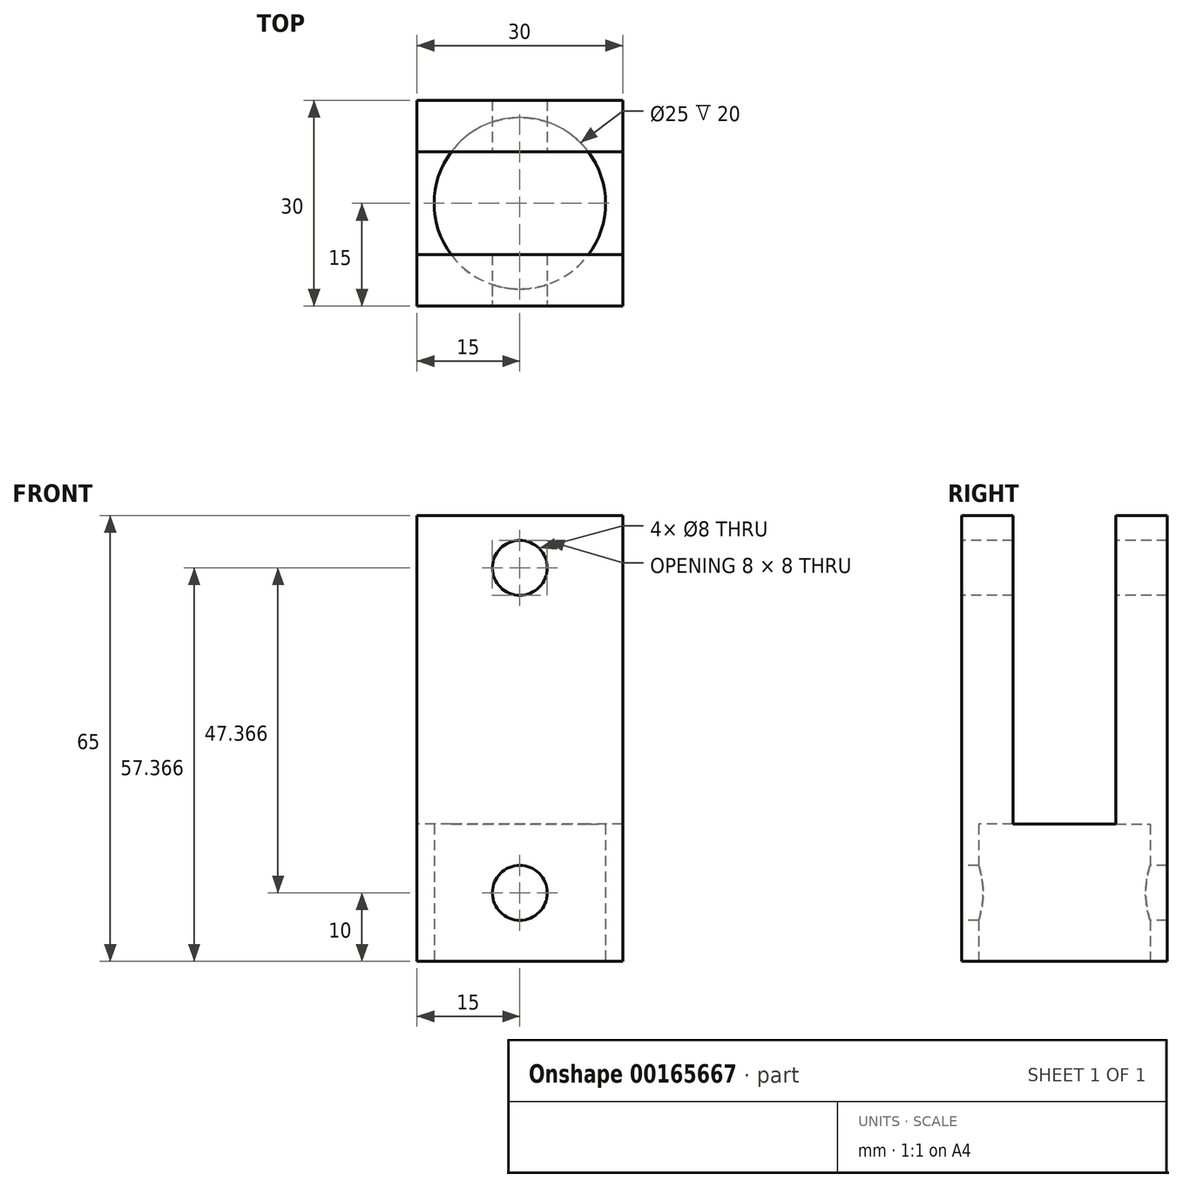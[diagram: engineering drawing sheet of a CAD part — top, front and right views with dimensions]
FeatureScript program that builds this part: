
annotation { "Feature Type Name" : "Feature", "Feature Type Description" : "" }
export const myFeature = defineFeature(function(context is Context, id is Id, definition is map)
    precondition{}
    {
        {
            var Q0;
            Q0=qCreatedBy(makeId("Top.planeOp"),FACE);
            var sketch = newSketch(context, id + "F0", { "sketchPlane" : qUnion([Q0])});
            skLineSegment(sketch, "E0.bottom", {"start": v(15, -15) * mm, "end": v(-15, -15) * mm});
            skLineSegment(sketch, "E0.top", {"start": v(15, 15) * mm, "end": v(-15, 15) * mm});
            skLineSegment(sketch, "E0.left", {"start": v(15, -15) * mm, "end": v(15, 15) * mm});
            skLineSegment(sketch, "E0.right", {"start": v(-15, -15) * mm, "end": v(-15, 15) * mm});
            skPoint(sketch, "E0.middle", {"position": v(0, 0) * mm});
            skCircle(sketch, "E1", {"center": v(0, 0) * mm, "radius": 12.5 * mm});
            skSolve(sketch);
        }
        {
            var Q0;
            Q0=makeQuery(id+"F0.imprint","IMPRINT",FACE,{"disambiguationData":[TD([[makeQuery(id+"F0.imprint","IMPRINT",EDGE,{"derivedFrom":sQuery(id+"F0.wireOp",EDGE,"E0.bottom")}),-1.0]])]});
            var Q1;
            Q1=makeQuery(id+"F0.imprint","IMPRINT",FACE,{"disambiguationData":[TD([[makeQuery(id+"F0.imprint","IMPRINT",EDGE,{"derivedFrom":sQuery(id+"F0.wireOp",EDGE,"E1")}),1.0]])]});
            extrude(context, id + "F1", {"entities" : qUnion([Q0, Q1]), "depth" : 65 * mm, "offsetDistance" : 25 * mm});
        }
        {
            var Q0;
            Q0=makeQuery(id+"F1.opExtrude","CAP_FACE",FACE,{"disambiguationData":[OSD([sQuery(id+"F0.wireOp",EDGE,"E0.bottom"),sQuery(id+"F0.wireOp",EDGE,"E0.top"),sQuery(id+"F0.wireOp",EDGE,"E0.left"),sQuery(id+"F0.wireOp",EDGE,"E0.right")])],"isStart":false});
            var sketch = newSketch(context, id + "F2", { "sketchPlane" : qUnion([Q0])});
            skPoint(sketch, "E2.middle", {"position": v(0, 0) * mm});
            skLineSegment(sketch, "E3.bottom", {"start": v(15, -12.44) * mm, "end": v(15, -12.44) * mm});
            skLineSegment(sketch, "E3.top", {"start": v(17.5, -12.56) * mm, "end": v(17.5, -12.56) * mm});
            skLineSegment(sketch, "E4.bottom", {"start": v(17.5, -7.5) * mm, "end": v(-17.5, -7.5) * mm});
            skLineSegment(sketch, "E4.top", {"start": v(17.5, 7.5) * mm, "end": v(-17.5, 7.5) * mm});
            skLineSegment(sketch, "E4.left", {"start": v(17.5, -7.5) * mm, "end": v(17.5, 7.5) * mm});
            skLineSegment(sketch, "E4.right", {"start": v(-17.5, -7.5) * mm, "end": v(-17.5, 7.5) * mm});
            skSolve(sketch);
        }
        {
            var Q0;
            Q0=makeQuery(id+"F2.imprint","IMPRINT",FACE,{"disambiguationData":[TD([[makeQuery(id+"F2.imprint","IMPRINT",EDGE,{"derivedFrom":sQuery(id+"F2.wireOp",EDGE,"E4.bottom")}),-1.0]])]});
            extrude(context, id + "F3", {"entities" : qUnion([Q0]), "operationType" : NewBodyOperationType.REMOVE, "oppositeDirection" : true, "depth" : 45 * mm, "offsetDistance" : 25 * mm});
        }
        {
            var Q0;
            Q0=makeQuery(id+"F1.opExtrude","SWEPT_FACE",FACE,{"disambiguationData":[OSD([sQuery(id+"F0.wireOp",EDGE,"E0.bottom")])]});
            var sketch = newSketch(context, id + "F4", { "sketchPlane" : qUnion([Q0])});
            skCircle(sketch, "E5", {"center": v(0, 10) * mm, "radius": 4 * mm});
            skCircle(sketch, "E6", {"center": v(0, 57.37) * mm, "radius": 4 * mm});
            skSolve(sketch);
        }
        {
            var Q0;
            Q0=makeQuery(id+"F4.imprint","IMPRINT",FACE,{"disambiguationData":[TD([[makeQuery(id+"F4.imprint","IMPRINT",EDGE,{"derivedFrom":sQuery(id+"F4.wireOp",EDGE,"E5")}),1.0]])]});
            var Q1;
            Q1=makeQuery(id+"F4.imprint","IMPRINT",FACE,{"disambiguationData":[TD([[makeQuery(id+"F4.imprint","IMPRINT",EDGE,{"derivedFrom":sQuery(id+"F4.wireOp",EDGE,"E6")}),1.0]])]});
            extrude(context, id + "F5", {"entities" : qUnion([Q0, Q1]), "operationType" : NewBodyOperationType.REMOVE, "endBound" : BoundingType.THROUGH_ALL, "oppositeDirection" : true, "depth" : 25 * mm, "offsetDistance" : 25 * mm});
        }
        {
            var Q0;
            Q0=makeQuery(id+"F0.imprint","IMPRINT",FACE,{"disambiguationData":[TD([[makeQuery(id+"F0.imprint","IMPRINT",EDGE,{"derivedFrom":sQuery(id+"F0.wireOp",EDGE,"E1")}),1.0]])]});
            var Q1;
            Q1=makeQuery(id+"F3.boolean.opBoolean","COPY",FACE,{"derivedFrom":makeQuery(id+"F3.opExtrude","CAP_FACE",FACE,{"disambiguationData":[OSD([sQuery(id+"F2.wireOp",EDGE,"E4.bottom"),sQuery(id+"F2.wireOp",EDGE,"E4.top"),sQuery(id+"F2.wireOp",EDGE,"E4.left"),sQuery(id+"F2.wireOp",EDGE,"E4.right")])],"isStart":false})});
            extrude(context, id + "F6", {"entities" : qUnion([Q0]), "operationType" : NewBodyOperationType.REMOVE, "endBound" : BoundingType.UP_TO_SURFACE, "depth" : 25 * mm, "endBoundEntityFace" : qUnion([Q1]), "offsetDistance" : 25 * mm});
        }
    });
